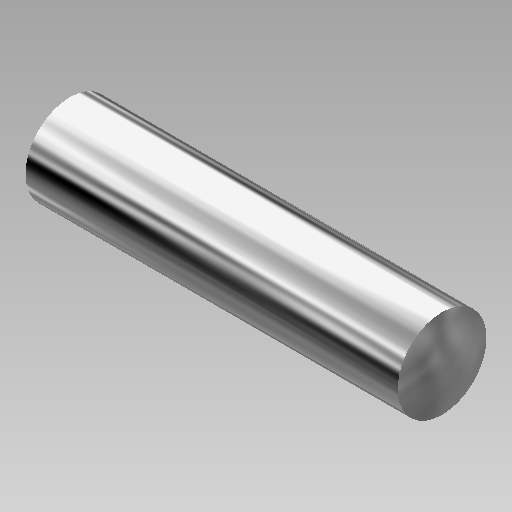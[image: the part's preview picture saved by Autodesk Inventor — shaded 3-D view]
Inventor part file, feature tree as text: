
AUTODESK INVENTOR PART (.ipt)
format: ipt  version: 2018.1 (Build 221171000, 171)  size: 128,000 bytes
history: native  units: in
note: dims shown in document units (in); Inventor stores cm internally (conversion verified against a paired STEP export)
features: revolve x1, sketch x1
ambient origin geometry x8: Origin, YZ Plane, XZ Plane, XY Plane, X Axis, Y Axis, Z Axis, Center Point
bodies: Solid1 (feature_tree)
feature tree (2):
  revolve  "Revolution1"  [1 undecoded]
  sketch  "Sketch1"  dims[d2=90.0deg]
note: 1 required parameter value undecoded (feature->parameter linkage not recoverable at this tier; creation-order binding heuristic only, values carry confidence <= 0.55)
